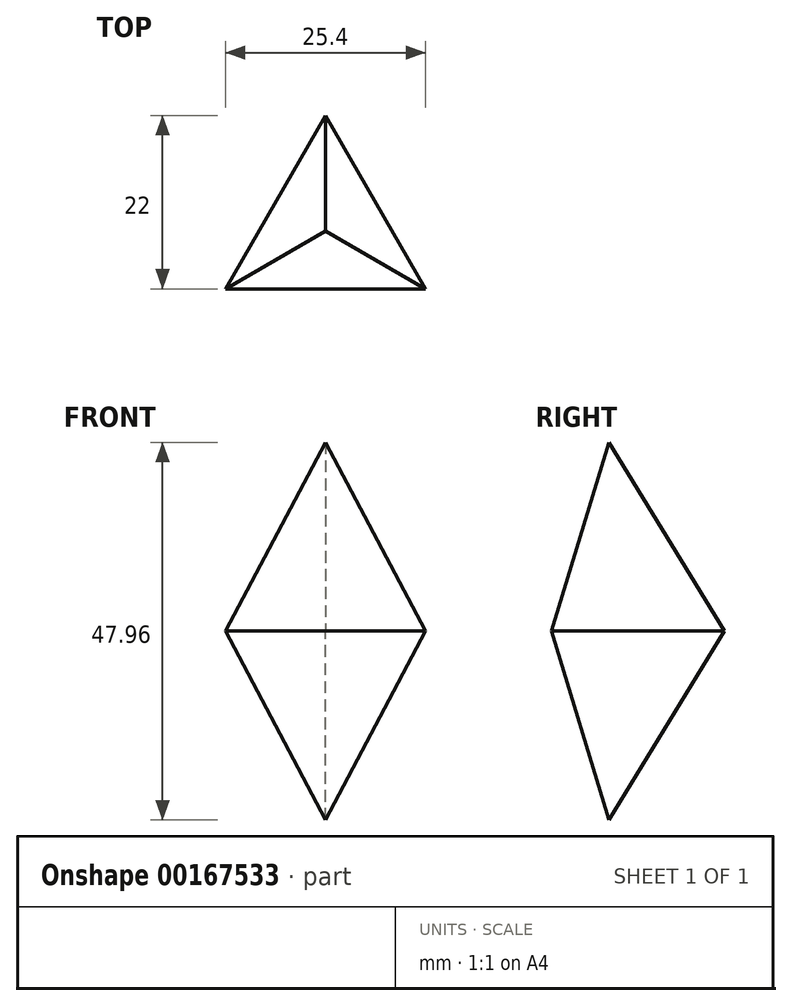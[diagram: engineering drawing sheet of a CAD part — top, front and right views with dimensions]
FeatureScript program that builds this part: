
annotation { "Feature Type Name" : "Feature", "Feature Type Description" : "" }
export const myFeature = defineFeature(function(context is Context, id is Id, definition is map)
    precondition{}
    {
        {
            var Q0;
            Q0=qCreatedBy(makeId("Top.planeOp"),FACE);
            var sketch = newSketch(context, id + "F0", { "sketchPlane" : qUnion([Q0])});
            skLineSegment(sketch, "E0", {"start": v(-12.7, 0) * mm, "end": v(12.7, 0) * mm});
            skLineSegment(sketch, "E1", {"start": v(12.7, 0) * mm, "end": v(0, 22) * mm});
            skLineSegment(sketch, "E2", {"start": v(0, 22) * mm, "end": v(-12.7, 0) * mm});
            skSolve(sketch);
        }
        {
            var Q0;
            Q0=makeQuery(id+"F0.imprint","IMPRINT",FACE,{"disambiguationData":[TD([[makeQuery(id+"F0.imprint","IMPRINT",EDGE,{"derivedFrom":sQuery(id+"F0.wireOp",EDGE,"E0")}),1.0]])]});
            extrude(context, id + "F1", {"entities" : qUnion([Q0]), "depth" : 25.4 * mm, "hasDraft" : true, "draftAngle" : 17 * degree, "draftPullDirection" : true});
        }
        {
            var Q0;
            Q0=makeQuery(id+"F1.opExtrude","CAP_FACE",FACE,{"disambiguationData":[OSD([sQuery(id+"F0.wireOp",EDGE,"E0"),sQuery(id+"F0.wireOp",EDGE,"E1"),sQuery(id+"F0.wireOp",EDGE,"E2")])],"isStart":true});
            extrude(context, id + "F2", {"entities" : qUnion([Q0]), "operationType" : NewBodyOperationType.ADD, "depth" : 25.4 * mm, "hasDraft" : true, "draftAngle" : 17 * degree, "draftPullDirection" : true});
        }
    });
